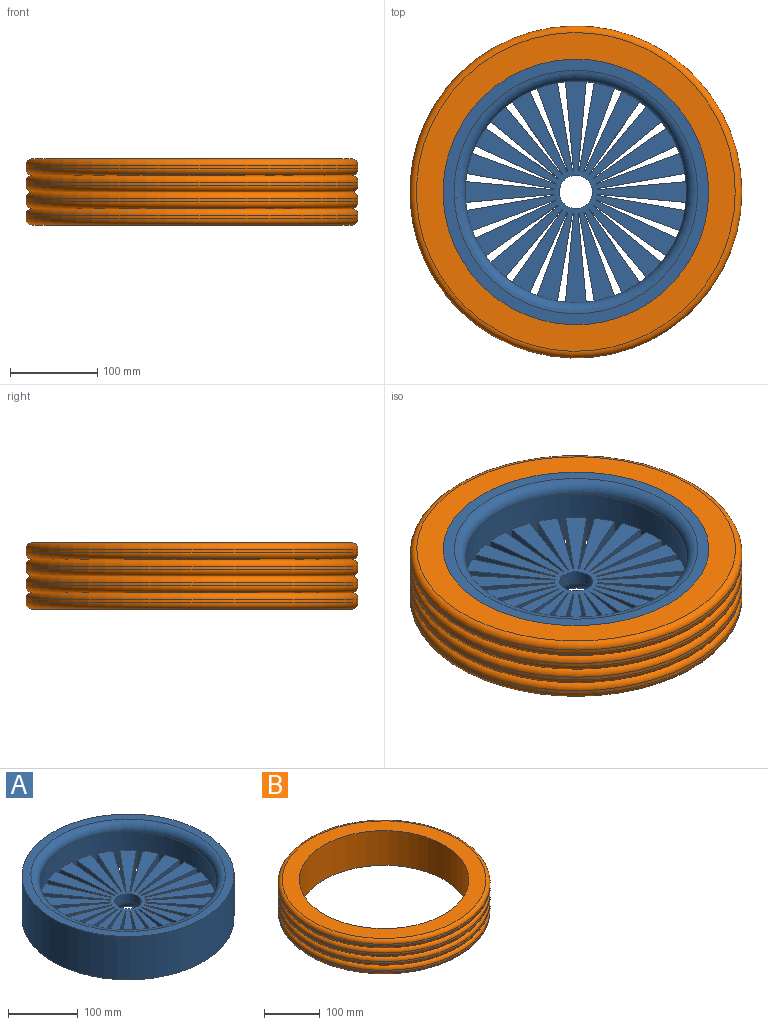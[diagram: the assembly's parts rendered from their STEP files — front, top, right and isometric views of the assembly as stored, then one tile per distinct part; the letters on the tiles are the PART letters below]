
ASSEMBLY  parts=2 mates=1
PART A: 128 faces, bbox 304.8x304.8x76.2 mm
  f0: cylinder r=127mm len=254mm, axis (0,0,-1), area 33256.4mm2, adj f26,f27,f28,f31,f32,f33,f34,f35
  f1: cylinder r=25.4mm len=27.62mm, axis (0,0,-1), area 33.2mm2, adj f31,f119,f123,f126
  f2: cylinder r=25.4mm len=27.62mm, axis (0,0,-1), area 33.2mm2, adj f31,f35,f122,f126
  f3: cylinder r=25.4mm len=27.62mm, axis (0,0,-1), area 33.2mm2, adj f31,f34,f38,f126
  f4: cylinder r=25.4mm len=27.62mm, axis (0,0,-1), area 33.2mm2, adj f31,f39,f43,f126
  f5: cylinder r=25.4mm len=27.62mm, axis (0,0,-1), area 33.2mm2, adj f31,f42,f46,f126
  f6: cylinder r=25.4mm len=27.62mm, axis (0,0,-1), area 33.2mm2, adj f31,f47,f51,f126
  f7: cylinder r=25.4mm len=27.62mm, axis (0,0,-1), area 33.2mm2, adj f31,f50,f54,f126
  f8: cylinder r=25.4mm len=27.62mm, axis (0,0,-1), area 33.2mm2, adj f31,f55,f59,f126
  f9: cylinder r=25.4mm len=27.62mm, axis (0,0,-1), area 33.2mm2, adj f31,f58,f62,f126
  f10: cylinder r=25.4mm len=27.62mm, axis (0,0,-1), area 33.2mm2, adj f31,f63,f67,f126
  f11: cylinder r=25.4mm len=27.62mm, axis (0,0,-1), area 33.2mm2, adj f31,f66,f70,f126
  f12: cylinder r=25.4mm len=27.62mm, axis (0,0,-1), area 33.2mm2, adj f31,f71,f75,f126
  f13: cylinder r=25.4mm len=27.62mm, axis (0,0,-1), area 33.2mm2, adj f31,f74,f78,f126
  f14: cylinder r=25.4mm len=27.62mm, axis (0,0,-1), area 33.2mm2, adj f31,f79,f83,f126
  f15: cylinder r=25.4mm len=27.62mm, axis (0,0,-1), area 33.2mm2, adj f31,f82,f86,f126
  f16: cylinder r=25.4mm len=27.62mm, axis (0,0,-1), area 33.2mm2, adj f31,f87,f91,f126
  f17: cylinder r=25.4mm len=27.62mm, axis (0,0,-1), area 33.2mm2, adj f31,f90,f94,f126
  f18: cylinder r=25.4mm len=27.62mm, axis (0,0,-1), area 33.2mm2, adj f31,f95,f99,f126
  f19: cylinder r=25.4mm len=27.62mm, axis (0,0,-1), area 33.2mm2, adj f31,f106,f110,f126
  f20: cylinder r=25.4mm len=27.62mm, axis (0,0,-1), area 33.2mm2, adj f31,f98,f102,f126
  f21: cylinder r=25.4mm len=27.62mm, axis (0,0,-1), area 33.2mm2, adj f28,f31,f103,f126
  f22: cylinder r=25.4mm len=27.62mm, axis (0,0,-1), area 33.2mm2, adj f27,f31,f107,f126
  f23: cylinder r=25.4mm len=27.62mm, axis (0,0,-1), area 33.2mm2, adj f31,f114,f118,f126
  f24: cylinder r=152.4mm len=304.8mm, axis (0,0,-1), area 72965.9mm2, adj f25,f26
  f25: plane 304.8x304.8mm, normal (0,0,1), area 11654.3mm2, adj f24,f127
  f26: plane 304.8x304.8mm, normal (0,0,-1), area 47311.7mm2, adj f0,f24,f32,f33,f36,f37,f40,f41
  f27: plane 101.18x28.35mm, normal (1,-0.09,0), area 2879.7mm2, adj f0,f22,f31,f33,f126
  f28: plane 101.18x28.35mm, normal (-1,-0.09,0), area 2879.7mm2, adj f0,f21,f31,f32,f126
  f29: cylinder r=25.4mm len=27.62mm, axis (0,0,-1), area 33.2mm2, adj f31,f111,f115,f126
  f30: cylinder r=19.05mm len=38.1mm, axis (0,0,-1), area 1824.1mm2, adj f31,f126
  f31: plane 254x254mm, normal (0,0,1), area 36733.8mm2, adj f0,f1,f2,f3,f4,f5,f6,f7
  f32: plane 100.26x10.63mm, normal (-0.7,-0.06,-0.71), area 295.6mm2, adj f0,f26,f28,f126
  f33: plane 100.26x10.63mm, normal (0.7,-0.06,-0.71), area 295.6mm2, adj f0,f26,f27,f126
  f34: plane 101.18x28.35mm, normal (-0.09,-1,0), area 2879.7mm2, adj f0,f3,f31,f36,f126
  f35: plane 101.18x28.35mm, normal (-0.09,1,0), area 2879.7mm2, adj f0,f2,f31,f37,f126
  f36: plane 100.26x10.63mm, normal (-0.06,-0.7,-0.71), area 295.6mm2, adj f0,f26,f34,f126
  f37: plane 100.26x10.63mm, normal (-0.06,0.7,-0.71), area 295.6mm2, adj f0,f26,f35,f126
  f38: plane 100.13x28.35mm, normal (0.17,0.99,0), area 2879.7mm2, adj f0,f3,f31,f41,f126
  f39: plane 95.34x35.11mm, normal (-0.35,-0.94,0), area 2879.7mm2, adj f0,f4,f31,f40,f126
  f40: plane 95.02x35mm, normal (-0.24,-0.66,-0.71), area 295.6mm2, adj f0,f26,f39,f126
  f41: plane 99.03x19.17mm, normal (0.12,0.7,-0.71), area 295.6mm2, adj f0,f26,f38,f126
  f42: plane 83.01x58.59mm, normal (-0.58,-0.82,0), area 2879.7mm2, adj f0,f5,f31,f44,f126
  f43: plane 92.25x42.59mm, normal (0.42,0.91,0), area 2879.7mm2, adj f0,f4,f31,f45,f126
  f44: plane 83.32x57.95mm, normal (-0.41,-0.58,-0.71), area 295.6mm2, adj f0,f26,f42,f126
  f45: plane 91.24x44.05mm, normal (0.3,0.64,-0.71), area 295.6mm2, adj f0,f26,f43,f126
  f46: plane 78.08x65.01mm, normal (0.64,0.77,0), area 2879.7mm2, adj f0,f5,f31,f49,f126
  f47: plane 78.08x65.01mm, normal (-0.77,-0.64,0), area 2879.7mm2, adj f0,f6,f31,f48,f126
  f48: plane 77.23x65.93mm, normal (-0.54,-0.45,-0.71), area 295.6mm2, adj f0,f26,f47,f126
  f49: plane 77.23x65.93mm, normal (0.45,0.54,-0.71), area 295.6mm2, adj f0,f26,f46,f126
  f50: plane 92.25x42.59mm, normal (-0.91,-0.42,0), area 2879.7mm2, adj f0,f7,f31,f52,f126
  f51: plane 83.01x58.59mm, normal (0.82,0.58,0), area 2879.7mm2, adj f0,f6,f31,f53,f126
  f52: plane 91.24x44.05mm, normal (-0.64,-0.3,-0.71), area 295.6mm2, adj f0,f26,f50,f126
  f53: plane 83.32x57.95mm, normal (0.58,0.41,-0.71), area 295.6mm2, adj f0,f26,f51,f126
  f54: plane 95.34x35.11mm, normal (0.94,0.35,0), area 2879.7mm2, adj f0,f7,f31,f57,f126
  f55: plane 100.13x28.35mm, normal (-0.99,-0.17,0), area 2879.7mm2, adj f0,f8,f31,f56,f126
  f56: plane 99.03x19.17mm, normal (-0.7,-0.12,-0.71), area 295.6mm2, adj f0,f26,f55,f126
  f57: plane 95.02x34.99mm, normal (0.66,0.24,-0.71), area 295.6mm2, adj f0,f26,f54,f126
  f58: plane 101.18x28.35mm, normal (-1,0.09,0), area 2879.7mm2, adj f0,f9,f31,f60,f126
  f59: plane 101.18x28.35mm, normal (1,0.09,0), area 2879.7mm2, adj f0,f8,f31,f61,f126
  f60: plane 100.26x10.63mm, normal (-0.7,0.06,-0.71), area 295.6mm2, adj f0,f26,f58,f126
  f61: plane 100.26x10.63mm, normal (0.7,0.06,-0.71), area 295.6mm2, adj f0,f26,f59,f126
  f62: plane 100.13x28.35mm, normal (0.99,-0.17,0), area 2879.7mm2, adj f0,f9,f31,f65,f126
  f63: plane 95.34x35.11mm, normal (-0.94,0.35,0), area 2879.7mm2, adj f0,f10,f31,f64,f126
  f64: plane 95.02x35mm, normal (-0.66,0.24,-0.71), area 295.6mm2, adj f0,f26,f63,f126
  f65: plane 99.03x19.17mm, normal (0.7,-0.12,-0.71), area 295.6mm2, adj f0,f26,f62,f126
  f66: plane 83.01x58.59mm, normal (-0.82,0.58,0), area 2879.7mm2, adj f0,f11,f31,f68,f126
  f67: plane 92.25x42.59mm, normal (0.91,-0.42,0), area 2879.7mm2, adj f0,f10,f31,f69,f126
  f68: plane 83.32x57.95mm, normal (-0.58,0.41,-0.71), area 295.6mm2, adj f0,f26,f66,f126
  f69: plane 91.24x44.05mm, normal (0.64,-0.3,-0.71), area 295.6mm2, adj f0,f26,f67,f126
  f70: plane 78.08x65.01mm, normal (0.77,-0.64,0), area 2879.7mm2, adj f0,f11,f31,f73,f126
  f71: plane 78.08x65.01mm, normal (-0.64,0.77,0), area 2879.7mm2, adj f0,f12,f31,f72,f126
  f72: plane 77.23x65.93mm, normal (-0.45,0.54,-0.71), area 295.6mm2, adj f0,f26,f71,f126
  f73: plane 77.23x65.93mm, normal (0.54,-0.45,-0.71), area 295.6mm2, adj f0,f26,f70,f126
  f74: plane 92.25x42.59mm, normal (-0.42,0.91,0), area 2879.7mm2, adj f0,f13,f31,f76,f126
  f75: plane 83.01x58.59mm, normal (0.58,-0.82,0), area 2879.7mm2, adj f0,f12,f31,f77,f126
  f76: plane 91.24x44.05mm, normal (-0.3,0.64,-0.71), area 295.6mm2, adj f0,f26,f74,f126
  f77: plane 83.32x57.95mm, normal (0.41,-0.58,-0.71), area 295.6mm2, adj f0,f26,f75,f126
  f78: plane 95.34x35.11mm, normal (0.35,-0.94,0), area 2879.7mm2, adj f0,f13,f31,f81,f126
  f79: plane 100.13x28.35mm, normal (-0.17,0.99,0), area 2879.7mm2, adj f0,f14,f31,f80,f126
  f80: plane 99.03x19.17mm, normal (-0.12,0.7,-0.71), area 295.6mm2, adj f0,f26,f79,f126
  f81: plane 95.02x34.99mm, normal (0.24,-0.66,-0.71), area 295.6mm2, adj f0,f26,f78,f126
  f82: plane 101.18x28.35mm, normal (0.09,1,0), area 2879.7mm2, adj f0,f15,f31,f84,f126
  f83: plane 101.18x28.35mm, normal (0.09,-1,0), area 2879.7mm2, adj f0,f14,f31,f85,f126
  f84: plane 100.26x10.63mm, normal (0.06,0.7,-0.71), area 295.6mm2, adj f0,f26,f82,f126
  f85: plane 100.26x10.63mm, normal (0.06,-0.7,-0.71), area 295.6mm2, adj f0,f26,f83,f126
  f86: plane 100.13x28.35mm, normal (-0.17,-0.99,0), area 2879.7mm2, adj f0,f15,f31,f89,f126
  f87: plane 95.34x35.11mm, normal (0.35,0.94,0), area 2879.7mm2, adj f0,f16,f31,f88,f126
  f88: plane 95.02x35mm, normal (0.24,0.66,-0.71), area 295.6mm2, adj f0,f26,f87,f126
  f89: plane 99.03x19.17mm, normal (-0.12,-0.7,-0.71), area 295.6mm2, adj f0,f26,f86,f126
  f90: plane 83.01x58.59mm, normal (0.58,0.82,0), area 2879.7mm2, adj f0,f17,f31,f92,f126
  f91: plane 92.25x42.59mm, normal (-0.42,-0.91,0), area 2879.7mm2, adj f0,f16,f31,f93,f126
  f92: plane 83.32x57.95mm, normal (0.41,0.58,-0.71), area 295.6mm2, adj f0,f26,f90,f126
  f93: plane 91.24x44.05mm, normal (-0.3,-0.64,-0.71), area 295.6mm2, adj f0,f26,f91,f126
  f94: plane 78.08x65.01mm, normal (-0.64,-0.77,0), area 2879.7mm2, adj f0,f17,f31,f97,f126
  f95: plane 78.08x65.01mm, normal (0.77,0.64,0), area 2879.7mm2, adj f0,f18,f31,f96,f126
  f96: plane 77.23x65.93mm, normal (0.54,0.45,-0.71), area 295.6mm2, adj f0,f26,f95,f126
  f97: plane 77.23x65.93mm, normal (-0.45,-0.54,-0.71), area 295.6mm2, adj f0,f26,f94,f126
  f98: plane 92.25x42.59mm, normal (0.91,0.42,0), area 2879.7mm2, adj f0,f20,f31,f100,f126
  f99: plane 83.01x58.59mm, normal (-0.82,-0.58,0), area 2879.7mm2, adj f0,f18,f31,f101,f126
  f100: plane 91.24x44.05mm, normal (0.64,0.3,-0.71), area 295.6mm2, adj f0,f26,f98,f126
  f101: plane 83.32x57.95mm, normal (-0.58,-0.41,-0.71), area 295.6mm2, adj f0,f26,f99,f126
  f102: plane 95.34x35.11mm, normal (-0.94,-0.35,0), area 2879.7mm2, adj f0,f20,f31,f105,f126
  f103: plane 100.13x28.35mm, normal (0.99,0.17,0), area 2879.7mm2, adj f0,f21,f31,f104,f126
  f104: plane 99.03x19.17mm, normal (0.7,0.12,-0.71), area 295.6mm2, adj f0,f26,f103,f126
  f105: plane 95.02x34.99mm, normal (-0.66,-0.24,-0.71), area 295.6mm2, adj f0,f26,f102,f126
  f106: plane 95.34x35.11mm, normal (0.94,-0.35,0), area 2879.7mm2, adj f0,f19,f31,f109,f126
  f107: plane 100.13x28.35mm, normal (-0.99,0.17,0), area 2879.7mm2, adj f0,f22,f31,f108,f126
  f108: plane 99.03x19.17mm, normal (-0.7,0.12,-0.71), area 295.6mm2, adj f0,f26,f107,f126
  f109: plane 95.02x35mm, normal (0.66,-0.24,-0.71), area 295.6mm2, adj f0,f26,f106,f126
  f110: plane 92.25x42.59mm, normal (-0.91,0.42,0), area 2879.7mm2, adj f0,f19,f31,f113,f126
  f111: plane 83.01x58.59mm, normal (0.82,-0.58,0), area 2879.7mm2, adj f0,f29,f31,f112,f126
  f112: plane 83.32x57.95mm, normal (0.58,-0.41,-0.71), area 295.6mm2, adj f0,f26,f111,f126
  f113: plane 91.24x44.05mm, normal (-0.64,0.3,-0.71), area 295.6mm2, adj f0,f26,f110,f126
  f114: plane 78.08x65.01mm, normal (0.64,-0.77,0), area 2879.7mm2, adj f0,f23,f31,f117,f126
  f115: plane 78.08x65.01mm, normal (-0.77,0.64,0), area 2879.7mm2, adj f0,f29,f31,f116,f126
  f116: plane 77.23x65.93mm, normal (-0.54,0.45,-0.71), area 295.6mm2, adj f0,f26,f115,f126
  f117: plane 77.23x65.93mm, normal (0.45,-0.54,-0.71), area 295.6mm2, adj f0,f26,f114,f126
  f118: plane 83.01x58.59mm, normal (-0.58,0.82,0), area 2879.7mm2, adj f0,f23,f31,f120,f126
  f119: plane 92.25x42.59mm, normal (0.42,-0.91,0), area 2879.7mm2, adj f0,f1,f31,f121,f126
  f120: plane 83.32x57.95mm, normal (-0.41,0.58,-0.71), area 295.6mm2, adj f0,f26,f118,f126
  f121: plane 91.24x44.05mm, normal (0.3,-0.64,-0.71), area 295.6mm2, adj f0,f26,f119,f126
  f122: plane 100.13x28.35mm, normal (0.17,-0.99,0), area 2879.7mm2, adj f0,f2,f31,f125,f126
  f123: plane 95.34x35.11mm, normal (-0.35,0.94,0), area 2879.7mm2, adj f0,f1,f31,f124,f126
  f124: plane 95.02x34.99mm, normal (-0.24,0.66,-0.71), area 295.6mm2, adj f0,f26,f123,f126
  f125: plane 99.03x19.17mm, normal (0.12,-0.7,-0.71), area 295.6mm2, adj f0,f26,f122,f126
  f126: torus R=34.29mm, axis (0,0,1), area 2791.8mm2, adj f1,f2,f3,f4,f5,f6,f7,f8
  f127: torus R=139.7mm, axis (0,0,1), area 16497.1mm2, adj f0,f25
PART B: 15 faces, bbox 412.4x412.4x76.2 mm
  f0: cylinder r=152.4mm len=304.8mm, axis (0,0,-1), area 72965.9mm2, adj f2,f12
  f1: cylinder r=190.5mm len=381mm, axis (0,0,-1), area 4560.4mm2, adj f3,f4
  f2: plane 365.76x365.76mm, normal (0,0,-1), area 32105mm2, adj f0,f3
  f3: torus R=182.88mm, axis (0,0,1), area 14118.6mm2, adj f1,f2
  f4: torus R=182.88mm, axis (0,0,1), area 14118.6mm2, adj f1,f6
  f5: cylinder r=190.5mm len=381mm, axis (0,0,-1), area 4560.4mm2, adj f6,f7
  f6: torus R=182.88mm, axis (0,0,1), area 14118.6mm2, adj f4,f5
  f7: torus R=182.88mm, axis (0,0,1), area 14118.6mm2, adj f5,f9
  f8: cylinder r=190.5mm len=381mm, axis (0,0,-1), area 4560.4mm2, adj f9,f10
  f9: torus R=182.88mm, axis (0,0,1), area 14118.6mm2, adj f7,f8
  f10: torus R=182.88mm, axis (0,0,1), area 14118.6mm2, adj f8,f13
  f11: cylinder r=190.5mm len=381mm, axis (0,0,-1), area 4560.4mm2, adj f13,f14
  f12: plane 365.76x365.76mm, normal (0,0,1), area 32105mm2, adj f0,f14
  f13: torus R=182.88mm, axis (0,0,1), area 14118.6mm2, adj f10,f11
  f14: torus R=182.88mm, axis (0,0,1), area 14118.6mm2, adj f11,f12
PLACE A t=(0,0,-15.24)mm
PLACE B rot(axis=(1,0,0),180deg) t=(0,0,60.96)mm
MATE fastened B.f0 <-> A.f30  axis (0,0,1) through (0,0,60.96)mm
